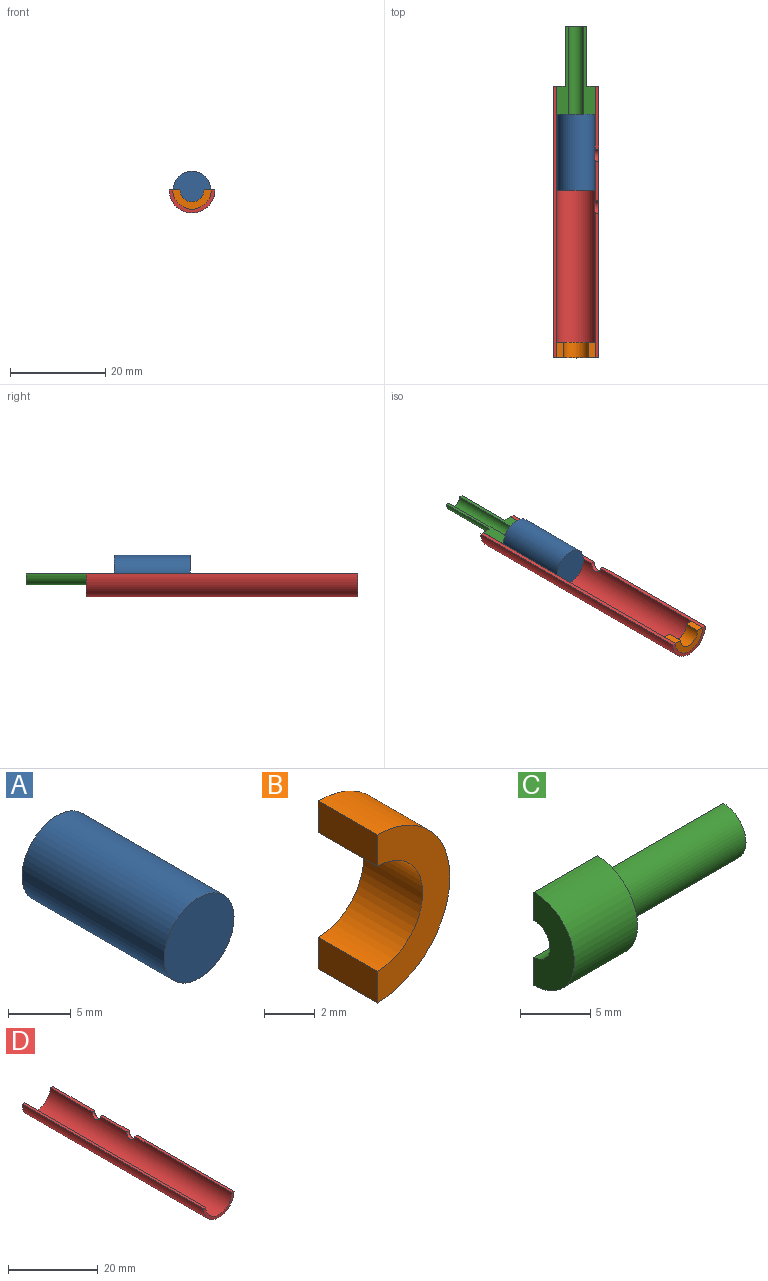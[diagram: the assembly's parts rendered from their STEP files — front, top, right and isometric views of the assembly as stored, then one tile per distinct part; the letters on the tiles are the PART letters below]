
ASSEMBLY  parts=4 mates=3
PART A: 3 faces, bbox 7.9x16x7.9 mm
  f0: cylinder r=3.94mm len=16mm, axis (0,1,0), area 395.8mm2, adj f1,f2
  f1: plane 7.87x7.87mm, normal (0,-1,0), area 48.7mm2, adj f0
  f2: plane 7.87x7.87mm, normal (0,1,0), area 48.7mm2, adj f0
PART B: 6 faces, bbox 4.1x3.3x8.1 mm
  f0: cylinder r=2.54mm len=5.08mm, axis (0,1,0), area 26.3mm2, adj f2,f3,f4,f5
  f1: cylinder r=4.06mm len=8.13mm, axis (0,1,0), area 42.2mm2, adj f2,f3,f4,f5
  f2: plane 8.13x4.06mm, normal (0,-1,0), area 15.8mm2, adj f0,f1,f4,f5
  f3: plane 8.13x4.06mm, normal (0,1,0), area 15.8mm2, adj f0,f1,f4,f5
  f4: plane 3.3x1.52mm, normal (-1,0,0), area 5mm2, adj f0,f1,f2,f3
  f5: plane 3.3x1.52mm, normal (-1,0,0), area 5mm2, adj f0,f1,f2,f3
PART C: 8 faces, bbox 19.1x4.1x8.1 mm
  f0: plane 8.13x4.06mm, normal (-1,0,0), area 21.9mm2, adj f1,f5,f6,f7
  f1: cylinder r=1.6mm len=19.05mm, axis (-1,0,0), area 95.8mm2, adj f0,f2,f6,f7
  f2: plane 4.57x2.29mm, normal (1,0,0), area 4.2mm2, adj f1,f3,f6,f7
  f3: cylinder r=2.29mm len=12.7mm, axis (-1,0,0), area 91.2mm2, adj f2,f4,f6,f7
  f4: plane 8.13x4.06mm, normal (1,0,0), area 17.7mm2, adj f3,f5,f6,f7
  f5: cylinder r=4.06mm len=8.13mm, axis (-1,0,0), area 81.1mm2, adj f0,f4,f6,f7
  f6: plane 19.05x2.46mm, normal (0,1,0), area 24.4mm2, adj f0,f1,f2,f3,f4,f5
  f7: plane 19.05x2.46mm, normal (0,1,0), area 24.4mm2, adj f0,f1,f2,f3,f4,f5
PART D: 10 faces, bbox 9.7x57.2x4.8 mm
  f0: cylinder r=4.06mm len=57.15mm, axis (0,1,0), area 724.3mm2, adj f2,f3,f4,f5,f6,f7,f8,f9
  f1: cylinder r=4.83mm len=57.15mm, axis (0,1,0), area 861.2mm2, adj f2,f3,f4,f5,f6,f7,f8,f9
  f2: plane 9.65x4.83mm, normal (0,-1,0), area 10.6mm2, adj f0,f1,f8,f9
  f3: plane 9.65x4.83mm, normal (0,1,0), area 10.6mm2, adj f0,f1,f6,f9
  f4: cylinder r=1.3mm len=2.6mm, axis (1,0,0), area 3.2mm2, adj f0,f1,f7,f8
  f5: cylinder r=1.29mm len=2.58mm, axis (1,0,0), area 3.2mm2, adj f0,f1,f6,f7
  f6: plane 13.19x0.76mm, normal (0,0,1), area 10mm2, adj f0,f1,f3,f5
  f7: plane 8.33x0.76mm, normal (0,0,1), area 6.3mm2, adj f0,f1,f4,f5
  f8: plane 30.45x0.76mm, normal (0,0,1), area 23.2mm2, adj f0,f1,f2,f4
  f9: plane 57.15x0.76mm, normal (0,0,1), area 43.5mm2, adj f0,f1,f2,f3
PLACE A t=(-16.55,5.44,-9.24)mm
PLACE B rot(axis=(0,1,0),90deg) t=(-16.55,-42.57,-9.24)mm
PLACE C rot(axis=(0.58,0.58,0.58),120deg) t=(-16.55,4.93,-9.24)mm
PLACE D t=(-16.55,11.28,-9.24)mm fixed
MATE fastened C.f1 <-> D.f0  axis (0,1,0) through (-16.55,11.28,-9.24)mm
MATE fastened B.f1 <-> D.f0  axis (0,-1,0) through (-16.55,-45.87,-9.24)mm
MATE slider A.f0 <-> D.f0  axis (0,1,0) through (-16.55,5.44,-9.24)mm
